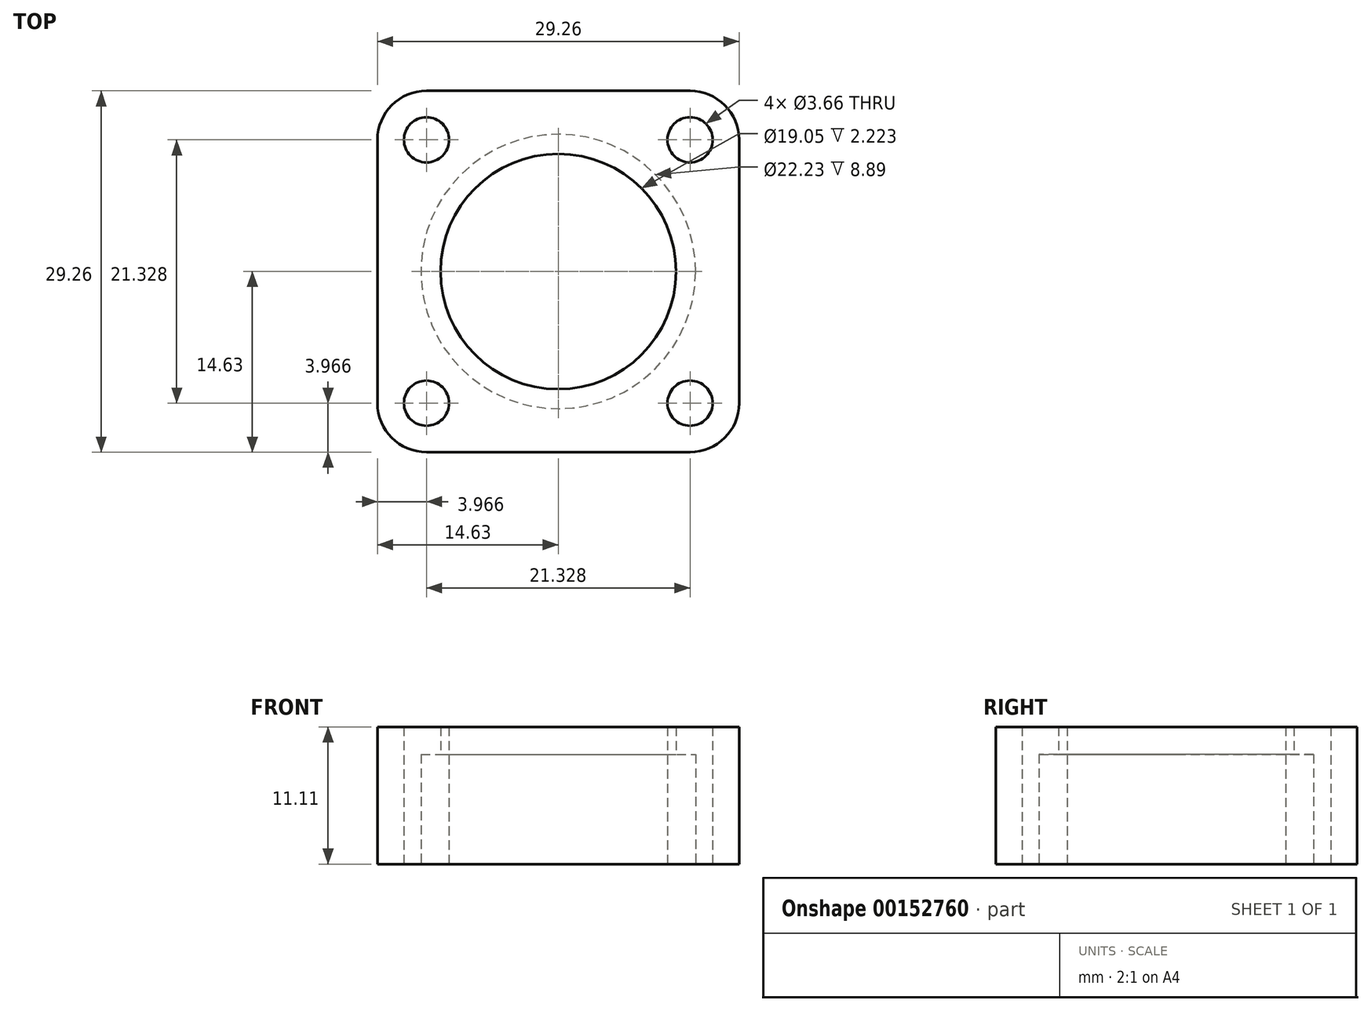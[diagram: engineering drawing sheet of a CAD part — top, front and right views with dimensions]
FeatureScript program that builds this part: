
annotation { "Feature Type Name" : "Feature", "Feature Type Description" : "" }
export const myFeature = defineFeature(function(context is Context, id is Id, definition is map)
    precondition{}
    {
        {
            var Q0;
            Q0=qCreatedBy(makeId("Top.planeOp"),FACE);
            var sketch = newSketch(context, id + "F0", { "sketchPlane" : qUnion([Q0])});
            skCircle(sketch, "E0", {"center": v(0, 0) * mm, "radius": 11.11 * mm, "construction": true});
            skLineSegment(sketch, "E1", {"start": v(0, 0) * mm, "end": v(0, -14.63) * mm, "construction": true});
            skLineSegment(sketch, "E2.bottom", {"start": v(14.63, -14.63) * mm, "end": v(-14.63, -14.63) * mm});
            skLineSegment(sketch, "E2.top", {"start": v(14.63, 14.63) * mm, "end": v(-14.63, 14.63) * mm});
            skLineSegment(sketch, "E2.left", {"start": v(14.63, -14.63) * mm, "end": v(14.63, 14.63) * mm});
            skLineSegment(sketch, "E2.right", {"start": v(-14.63, -14.63) * mm, "end": v(-14.63, 14.63) * mm});
            skLineSegment(sketch, "E3.bottom", {"start": v(-10.66, 10.66) * mm, "end": v(10.66, 10.66) * mm, "construction": true});
            skLineSegment(sketch, "E3.top", {"start": v(-10.66, -10.66) * mm, "end": v(10.66, -10.66) * mm, "construction": true});
            skLineSegment(sketch, "E3.left", {"start": v(-10.66, 10.66) * mm, "end": v(-10.66, -10.66) * mm, "construction": true});
            skLineSegment(sketch, "E3.right", {"start": v(10.66, 10.66) * mm, "end": v(10.66, -10.66) * mm, "construction": true});
            skCircle(sketch, "E4", {"center": v(-10.66, 10.66) * mm, "radius": 3.97 * mm, "construction": true});
            skLineSegment(sketch, "E5", {"start": v(0, 0) * mm, "end": v(0, 14.63) * mm, "construction": true});
            skCircle(sketch, "E6", {"center": v(-10.66, 10.66) * mm, "radius": 1.83 * mm});
            skCircle(sketch, "E7", {"center": v(10.66, 10.66) * mm, "radius": 1.83 * mm});
            skCircle(sketch, "E8", {"center": v(10.66, -10.66) * mm, "radius": 1.83 * mm});
            skCircle(sketch, "E9", {"center": v(-10.66, -10.66) * mm, "radius": 1.83 * mm});
            skCircle(sketch, "E10", {"center": v(0, 0) * mm, "radius": 9.53 * mm});
            skSolve(sketch);
        }
        {
            var Q0;
            Q0 = qSketchRegion(id + "F0", true);
            extrude(context, id + "F1", {"entities" : qUnion([Q0]), "depth" : 11.1 * mm});
        }
        {
            var Q0;
            Q0=makeQuery(id+"F1.opExtrude","SWEPT_EDGE",EDGE,{"disambiguationData":[OSD([sQuery(id+"F0.wireOp",EDGE,"E2.top"),sQuery(id+"F0.wireOp",EDGE,"E2.right")])]});
            var Q1;
            Q1=makeQuery(id+"F1.opExtrude","SWEPT_EDGE",EDGE,{"disambiguationData":[OSD([sQuery(id+"F0.wireOp",EDGE,"E2.bottom"),sQuery(id+"F0.wireOp",EDGE,"E2.right")])]});
            var Q2;
            Q2=makeQuery(id+"F1.opExtrude","SWEPT_EDGE",EDGE,{"disambiguationData":[OSD([sQuery(id+"F0.wireOp",EDGE,"E2.bottom"),sQuery(id+"F0.wireOp",EDGE,"E2.left")])]});
            var Q3;
            Q3=makeQuery(id+"F1.opExtrude","SWEPT_EDGE",EDGE,{"disambiguationData":[OSD([sQuery(id+"F0.wireOp",EDGE,"E2.top"),sQuery(id+"F0.wireOp",EDGE,"E2.left")])]});
            fillet(context, id + "F2", {"entities" : qUnion([Q0, Q1, Q2, Q3]), "radius" : 3.97 * mm, "tangentPropagation" : true, "allowEdgeOverflow" : false});
        }
        {
            var Q0;
            Q0=makeQuery(id+"F1.opExtrude","CAP_FACE",FACE,{"disambiguationData":[OSD([sQuery(id+"F0.wireOp",EDGE,"E2.bottom"),sQuery(id+"F0.wireOp",EDGE,"E2.top"),sQuery(id+"F0.wireOp",EDGE,"E2.left"),sQuery(id+"F0.wireOp",EDGE,"E2.right"),sQuery(id+"F0.wireOp",EDGE,"E6"),sQuery(id+"F0.wireOp",EDGE,"E7"),sQuery(id+"F0.wireOp",EDGE,"E8"),sQuery(id+"F0.wireOp",EDGE,"E9"),sQuery(id+"F0.wireOp",EDGE,"E10")])],"isStart":true});
            var sketch = newSketch(context, id + "F3", { "sketchPlane" : qUnion([Q0])});
            skCircle(sketch, "E11", {"center": v(0, 0) * mm, "radius": 11.11 * mm});
            skSolve(sketch);
        }
        {
            var Q0;
            Q0 = qSketchRegion(id + "F3", true);
            extrude(context, id + "F4", {"entities" : qUnion([Q0]), "operationType" : NewBodyOperationType.REMOVE, "oppositeDirection" : true, "depth" : 8.9 * mm});
        }
    });
